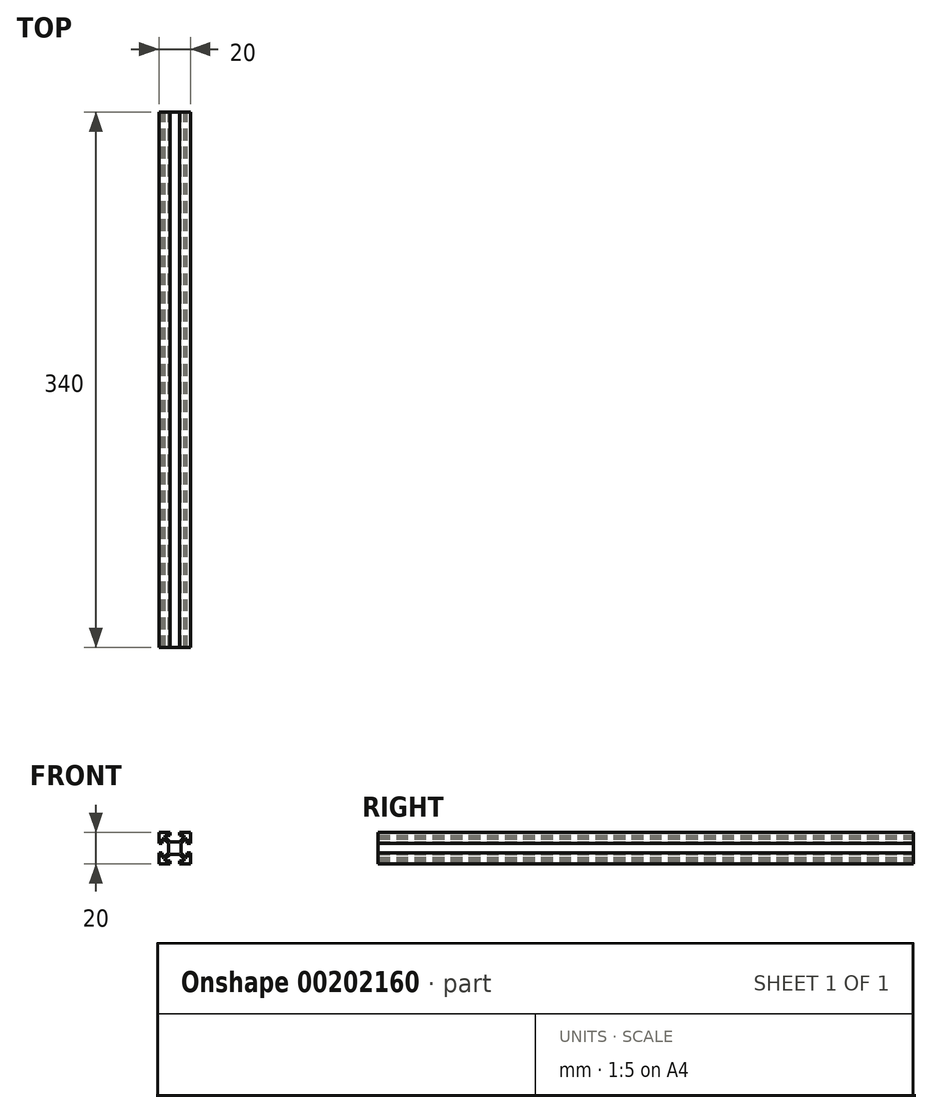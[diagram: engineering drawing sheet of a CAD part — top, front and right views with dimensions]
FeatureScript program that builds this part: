
annotation { "Feature Type Name" : "Feature", "Feature Type Description" : "" }
export const myFeature = defineFeature(function(context is Context, id is Id, definition is map)
    precondition{}
    {
        {
            var Q0;
            Q0=qCreatedBy(makeId("Front.planeOp"),FACE);
            var sketch = newSketch(context, id + "F0", { "sketchPlane" : qUnion([Q0])});
            skLineSegment(sketch, "E0", {"start": v(-48.23, 44.73) * mm, "end": v(-46.23, 44.73) * mm});
            skLineSegment(sketch, "E1", {"start": v(-46.23, 44.73) * mm, "end": v(-46.23, 47.73) * mm});
            skLineSegment(sketch, "E2", {"start": v(-46.23, 47.73) * mm, "end": v(-45.23, 47.73) * mm});
            skLineSegment(sketch, "E3", {"start": v(-45.23, 47.73) * mm, "end": v(-42.23, 44.73) * mm});
            skLineSegment(sketch, "E4", {"start": v(-42.23, 44.73) * mm, "end": v(-42.23, 38.73) * mm});
            skLineSegment(sketch, "E5", {"start": v(-42.23, 38.73) * mm, "end": v(-45.23, 35.73) * mm});
            skLineSegment(sketch, "E6", {"start": v(-45.23, 35.73) * mm, "end": v(-46.23, 35.73) * mm});
            skLineSegment(sketch, "E7", {"start": v(-46.23, 35.73) * mm, "end": v(-46.23, 38.73) * mm});
            skLineSegment(sketch, "E8", {"start": v(-46.23, 38.73) * mm, "end": v(-48.23, 38.73) * mm});
            skLineSegment(sketch, "E9", {"start": v(-48.23, 38.73) * mm, "end": v(-48.23, 31.73) * mm});
            skLineSegment(sketch, "E10", {"start": v(-48.23, 31.73) * mm, "end": v(-41.23, 31.73) * mm});
            skLineSegment(sketch, "E11", {"start": v(-41.23, 31.73) * mm, "end": v(-41.23, 33.73) * mm});
            skLineSegment(sketch, "E12", {"start": v(-41.23, 33.73) * mm, "end": v(-44.23, 33.73) * mm});
            skLineSegment(sketch, "E13", {"start": v(-44.23, 33.73) * mm, "end": v(-44.23, 34.73) * mm});
            skLineSegment(sketch, "E14", {"start": v(-44.23, 34.73) * mm, "end": v(-41.23, 37.73) * mm});
            skLineSegment(sketch, "E15", {"start": v(-41.23, 37.73) * mm, "end": v(-35.23, 37.73) * mm});
            skLineSegment(sketch, "E16", {"start": v(-35.23, 37.73) * mm, "end": v(-32.23, 34.73) * mm});
            skLineSegment(sketch, "E17", {"start": v(-32.23, 34.73) * mm, "end": v(-32.23, 33.73) * mm});
            skLineSegment(sketch, "E18", {"start": v(-32.23, 33.73) * mm, "end": v(-35.23, 33.73) * mm});
            skLineSegment(sketch, "E19", {"start": v(-35.23, 33.73) * mm, "end": v(-35.23, 31.73) * mm});
            skLineSegment(sketch, "E20", {"start": v(-35.23, 31.73) * mm, "end": v(-28.23, 31.73) * mm});
            skLineSegment(sketch, "E21", {"start": v(-28.23, 31.73) * mm, "end": v(-28.23, 38.73) * mm});
            skLineSegment(sketch, "E22", {"start": v(-28.23, 38.73) * mm, "end": v(-30.23, 38.73) * mm});
            skLineSegment(sketch, "E23", {"start": v(-30.23, 38.73) * mm, "end": v(-30.23, 35.73) * mm});
            skLineSegment(sketch, "E24", {"start": v(-30.23, 35.73) * mm, "end": v(-31.23, 35.73) * mm});
            skLineSegment(sketch, "E25", {"start": v(-31.23, 35.73) * mm, "end": v(-34.23, 38.73) * mm});
            skLineSegment(sketch, "E26", {"start": v(-34.23, 38.73) * mm, "end": v(-34.23, 44.73) * mm});
            skLineSegment(sketch, "E27", {"start": v(-34.23, 44.73) * mm, "end": v(-31.23, 47.73) * mm});
            skLineSegment(sketch, "E28", {"start": v(-31.23, 47.73) * mm, "end": v(-30.23, 47.73) * mm});
            skLineSegment(sketch, "E29", {"start": v(-30.23, 47.73) * mm, "end": v(-30.23, 44.73) * mm});
            skLineSegment(sketch, "E30", {"start": v(-30.23, 44.73) * mm, "end": v(-28.23, 44.73) * mm});
            skLineSegment(sketch, "E31", {"start": v(-28.23, 44.73) * mm, "end": v(-28.23, 51.73) * mm});
            skLineSegment(sketch, "E32", {"start": v(-28.23, 51.73) * mm, "end": v(-35.23, 51.73) * mm});
            skLineSegment(sketch, "E33", {"start": v(-35.23, 51.73) * mm, "end": v(-35.23, 49.73) * mm});
            skLineSegment(sketch, "E34", {"start": v(-35.23, 49.73) * mm, "end": v(-32.23, 49.73) * mm});
            skLineSegment(sketch, "E35", {"start": v(-32.23, 49.73) * mm, "end": v(-32.23, 48.73) * mm});
            skLineSegment(sketch, "E36", {"start": v(-32.23, 48.73) * mm, "end": v(-35.23, 45.73) * mm});
            skLineSegment(sketch, "E37", {"start": v(-35.23, 45.73) * mm, "end": v(-41.23, 45.73) * mm});
            skLineSegment(sketch, "E38", {"start": v(-41.23, 45.73) * mm, "end": v(-44.23, 48.73) * mm});
            skLineSegment(sketch, "E39", {"start": v(-44.23, 48.73) * mm, "end": v(-44.23, 49.73) * mm});
            skLineSegment(sketch, "E40", {"start": v(-44.23, 49.73) * mm, "end": v(-41.23, 49.73) * mm});
            skLineSegment(sketch, "E41", {"start": v(-41.23, 49.73) * mm, "end": v(-41.23, 51.73) * mm});
            skLineSegment(sketch, "E42", {"start": v(-41.23, 51.73) * mm, "end": v(-48.23, 51.73) * mm});
            skLineSegment(sketch, "E43", {"start": v(-48.23, 51.73) * mm, "end": v(-48.23, 44.73) * mm});
            skSolve(sketch);
        }
        {
            var Q0;
            Q0=qSketchRegion(id+"F0",true);
            extrude(context, id + "F1", {"entities" : qUnion([Q0]), "depth" : 340 * mm});
        }
    });
